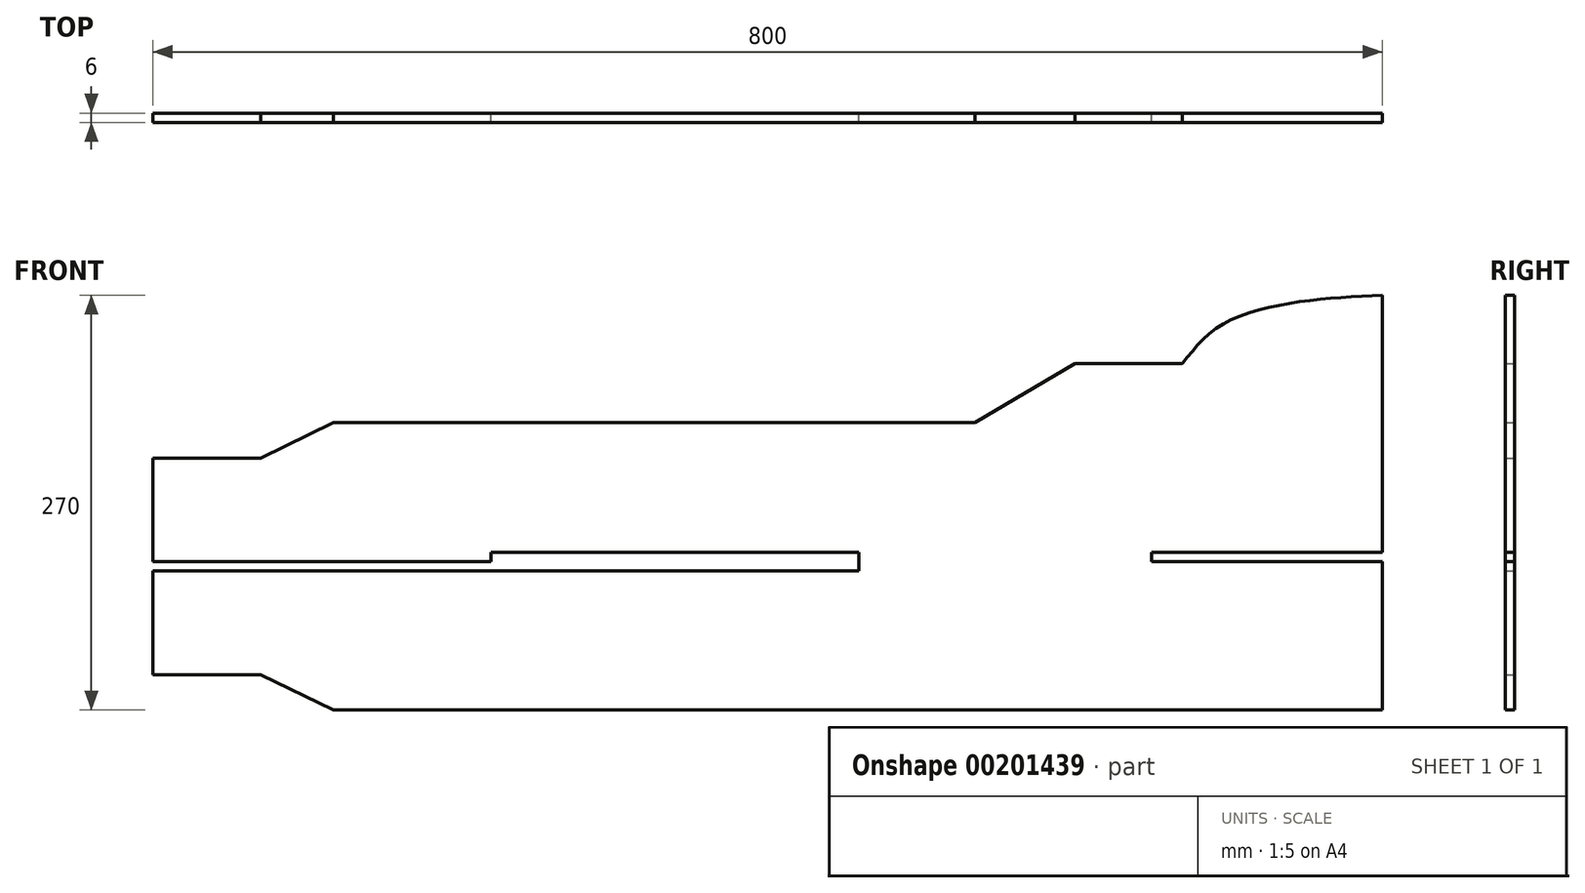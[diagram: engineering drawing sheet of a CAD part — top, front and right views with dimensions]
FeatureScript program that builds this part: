
annotation { "Feature Type Name" : "Feature", "Feature Type Description" : "" }
export const myFeature = defineFeature(function(context is Context, id is Id, definition is map)
    precondition{}
    {
        {
            var Q0;
            Q0=qCreatedBy(makeId("Front.planeOp"),FACE);
            var sketch = newSketch(context, id + "F0", { "sketchPlane" : qUnion([Q0])});
            skLineSegment(sketch, "E0", {"start": v(-254.12, 63.11) * mm, "end": v(-34.12, 63.11) * mm});
            skLineSegment(sketch, "E1", {"start": v(-254.12, 63.11) * mm, "end": v(-254.12, 130.61) * mm});
            skLineSegment(sketch, "E2", {"start": v(-254.12, 130.61) * mm, "end": v(-184.12, 130.61) * mm});
            skLineSegment(sketch, "E3", {"start": v(-184.12, 130.61) * mm, "end": v(-136.74, 153.67) * mm});
            skLineSegment(sketch, "E4", {"start": v(-136.74, 153.67) * mm, "end": v(280.88, 153.67) * mm});
            skLineSegment(sketch, "E5", {"start": v(280.88, 153.67) * mm, "end": v(345.88, 191.94) * mm});
            skLineSegment(sketch, "E6", {"start": v(345.88, 191.94) * mm, "end": v(415.88, 191.94) * mm});
            skLineSegment(sketch, "E7", {"start": v(-34.12, 63.11) * mm, "end": v(-34.12, 69.11) * mm});
            skLineSegment(sketch, "E8", {"start": v(-34.12, 69.11) * mm, "end": v(205.24, 69.11) * mm});
            skLineSegment(sketch, "E9", {"start": v(-469.05, 60.11) * mm, "end": v(757.76, 60.11) * mm, "construction": true});
            skLineSegment(sketch, "E10", {"start": v(205.24, 69.11) * mm, "end": v(205.24, 57.11) * mm});
            skLineSegment(sketch, "E11", {"start": v(205.24, 57.11) * mm, "end": v(-254.12, 57.11) * mm});
            skLineSegment(sketch, "E12", {"start": v(-254.12, 57.11) * mm, "end": v(-254.12, -10.39) * mm});
            skLineSegment(sketch, "E13", {"start": v(-254.12, -10.39) * mm, "end": v(-184.12, -10.39) * mm});
            skLineSegment(sketch, "E14.MirrorCS", {"start": v(-184.12, -10.39) * mm, "end": v(-136.74, -33.45) * mm});
            skLineSegment(sketch, "E15", {"start": v(545.88, 251.36) * mm, "end": v(545.88, -125.14) * mm, "construction": true});
            skLineSegment(sketch, "E16", {"start": v(-136.74, -33.45) * mm, "end": v(545.88, -33.45) * mm});
            skLineSegment(sketch, "E17", {"start": v(545.88, -33.45) * mm, "end": v(545.88, 236.55) * mm});
            skFitSpline(sketch, "E18", {"points": [v(415.88, 191.94) * mm, v(440.3, 216.67) * mm, v(489.27, 231.85) * mm, v(545.88, 236.55) * mm], "startDerivative": vector(72.67, 94.92) * mm, "endDerivative": vector(154.3, 7.63) * mm});
            skLineSegment(sketch, "E19", {"start": v(545.88, 63.11) * mm, "end": v(395.88, 63.11) * mm});
            skLineSegment(sketch, "E20", {"start": v(395.88, 63.11) * mm, "end": v(395.88, 69.11) * mm});
            skLineSegment(sketch, "E21", {"start": v(395.88, 69.11) * mm, "end": v(545.88, 69.11) * mm});
            skSolve(sketch);
        }
        {
            var Q0;
            Q0=makeQuery(id+"F0.imprint","IMPRINT",FACE,{"disambiguationData":[TD([[makeQuery(id+"F0.imprint","IMPRINT",EDGE,{"derivedFrom":sQuery(id+"F0.wireOp",EDGE,"E0")}),1.0]])]});
            extrude(context, id + "F1", {"entities" : qUnion([Q0]), "depth" : 6 * mm});
        }
    });
